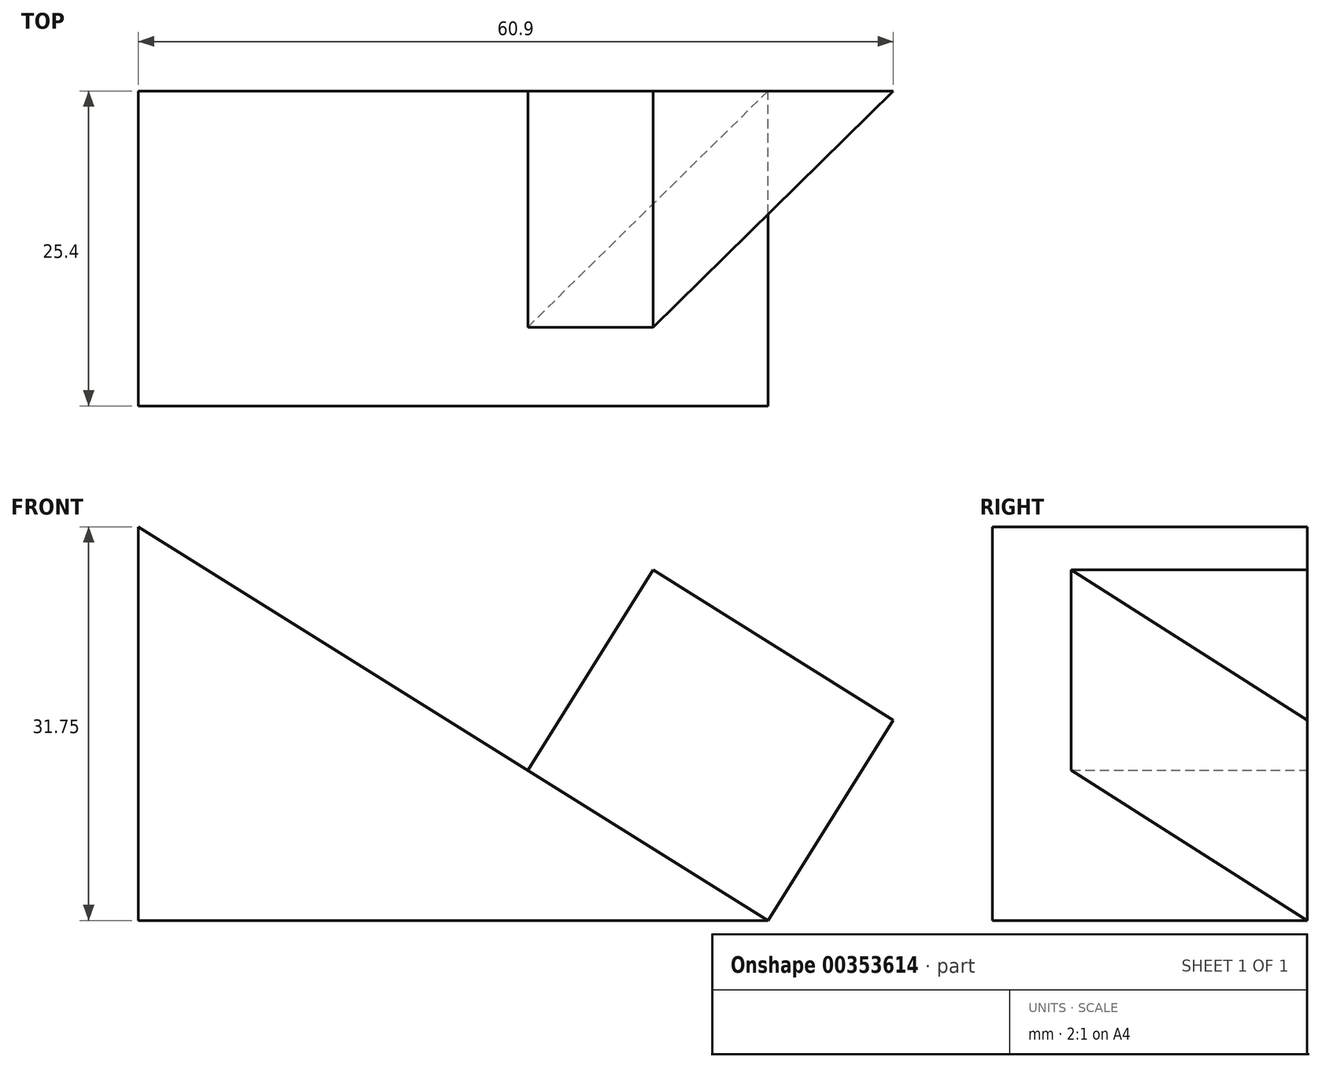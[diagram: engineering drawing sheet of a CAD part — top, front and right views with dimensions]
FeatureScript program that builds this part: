
annotation { "Feature Type Name" : "Feature", "Feature Type Description" : "" }
export const myFeature = defineFeature(function(context is Context, id is Id, definition is map)
    precondition{}
    {
        {
            var Q0;
            Q0=qCreatedBy(makeId("Front.planeOp"),FACE);
            var sketch = newSketch(context, id + "F0", { "sketchPlane" : qUnion([Q0])});
            skLineSegment(sketch, "E0", {"start": v(0, 0) * mm, "end": v(0, 31.75) * mm});
            skLineSegment(sketch, "E1", {"start": v(0, 31.75) * mm, "end": v(50.8, 0) * mm});
            skLineSegment(sketch, "E2", {"start": v(50.8, 0) * mm, "end": v(0, 0) * mm});
            skSolve(sketch);
        }
        {
            var Q0;
            Q0=makeQuery(id+"F0.imprint","IMPRINT",FACE,{"disambiguationData":[TD([[makeQuery(id+"F0.imprint","IMPRINT",EDGE,{"derivedFrom":sQuery(id+"F0.wireOp",EDGE,"E0")}),-1.0]])]});
            extrude(context, id + "F1", {"entities" : qUnion([Q0]), "depth" : 25.4 * mm});
        }
        {
            var Q0;
            Q0=makeQuery(id+"F1.opExtrude","SWEPT_FACE",FACE,{"disambiguationData":[OSD([sQuery(id+"F0.wireOp",EDGE,"E1")])]});
            var sketch = newSketch(context, id + "F2", { "sketchPlane" : qUnion([Q0])});
            skLineSegment(sketch, "E3", {"start": v(43.08, 0) * mm, "end": v(20.22, -19.05) * mm});
            skLineSegment(sketch, "E4", {"start": v(20.22, -19.05) * mm, "end": v(20.22, 0) * mm});
            skLineSegment(sketch, "E5", {"start": v(20.22, 0) * mm, "end": v(43.08, 0) * mm});
            skSolve(sketch);
        }
        {
            var Q0;
            Q0=makeQuery(id+"F2.imprint","IMPRINT",FACE,{"disambiguationData":[TD([[makeQuery(id+"F2.imprint","IMPRINT",EDGE,{"derivedFrom":sQuery(id+"F2.wireOp",EDGE,"E3")}),-1.0]])]});
            extrude(context, id + "F3", {"entities" : qUnion([Q0]), "operationType" : NewBodyOperationType.ADD, "depth" : 19.05 * mm});
        }
    });
